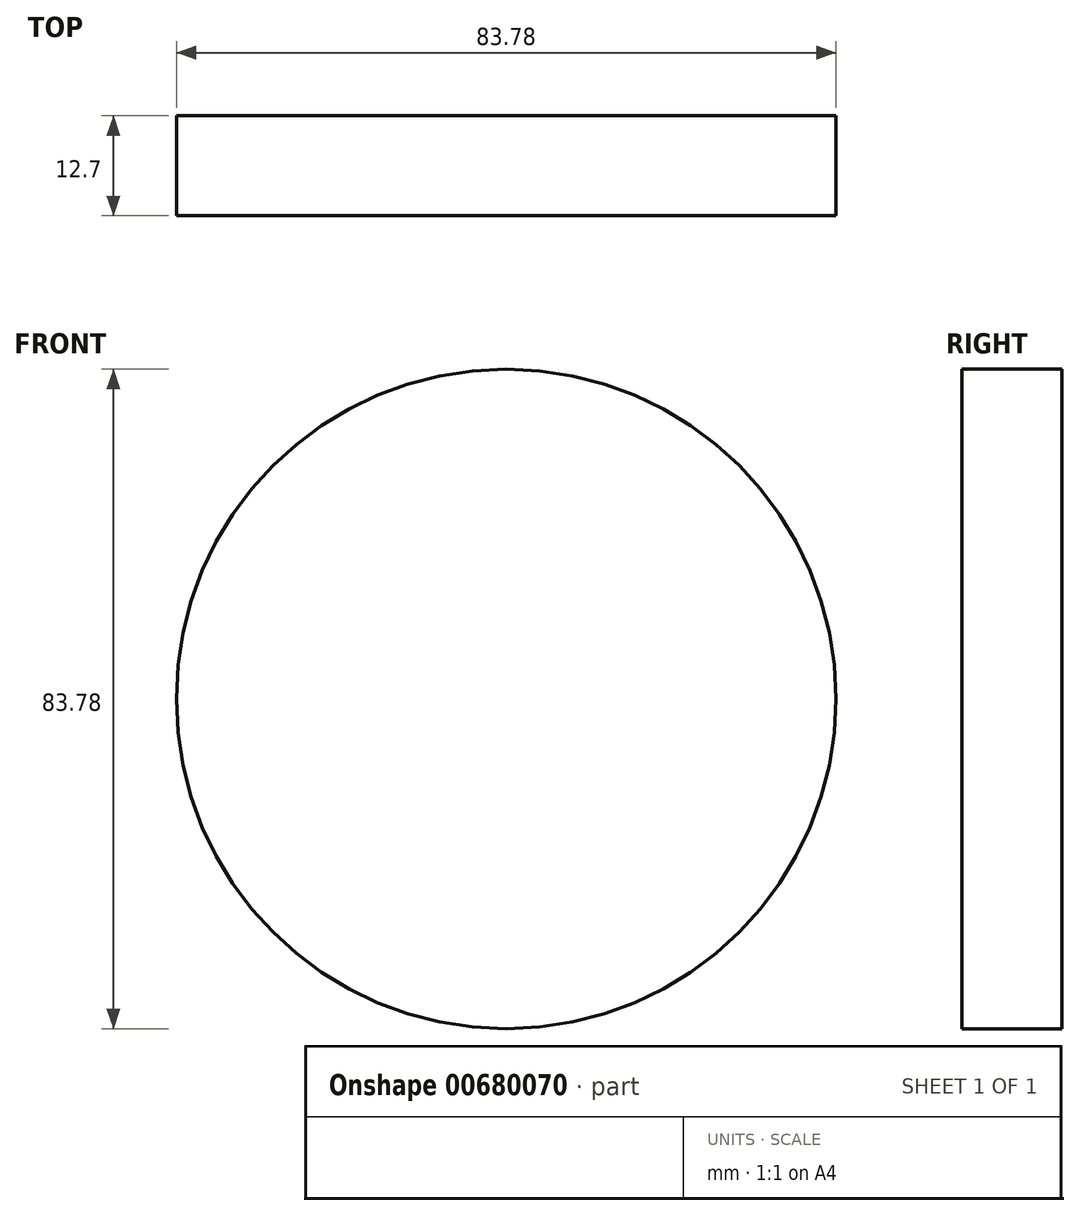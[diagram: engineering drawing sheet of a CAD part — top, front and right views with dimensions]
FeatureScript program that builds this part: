
annotation { "Feature Type Name" : "Feature", "Feature Type Description" : "" }
export const myFeature = defineFeature(function(context is Context, id is Id, definition is map)
    precondition{}
    {
        {
            var Q0;
            Q0=qCreatedBy(makeId("Front.planeOp"),FACE);
            var sketch = newSketch(context, id + "F0", { "sketchPlane" : qUnion([Q0])});
            skCircle(sketch, "E0", {"center": v(0, 0) * mm, "radius": 41.9 * mm});
            skSolve(sketch);
        }
        {
            var Q0;
            Q0=makeQuery(id+"F0.imprint","IMPRINT",FACE,{"disambiguationData":[TD([[makeQuery(id+"F0.imprint","IMPRINT",EDGE,{"derivedFrom":sQuery(id+"F0.wireOp",EDGE,"E0")}),1.0]])]});
            extrude(context, id + "F1", {"entities" : qUnion([Q0]), "depth" : 12.7 * mm, "offsetDistance" : 25.4 * mm});
        }
    });
